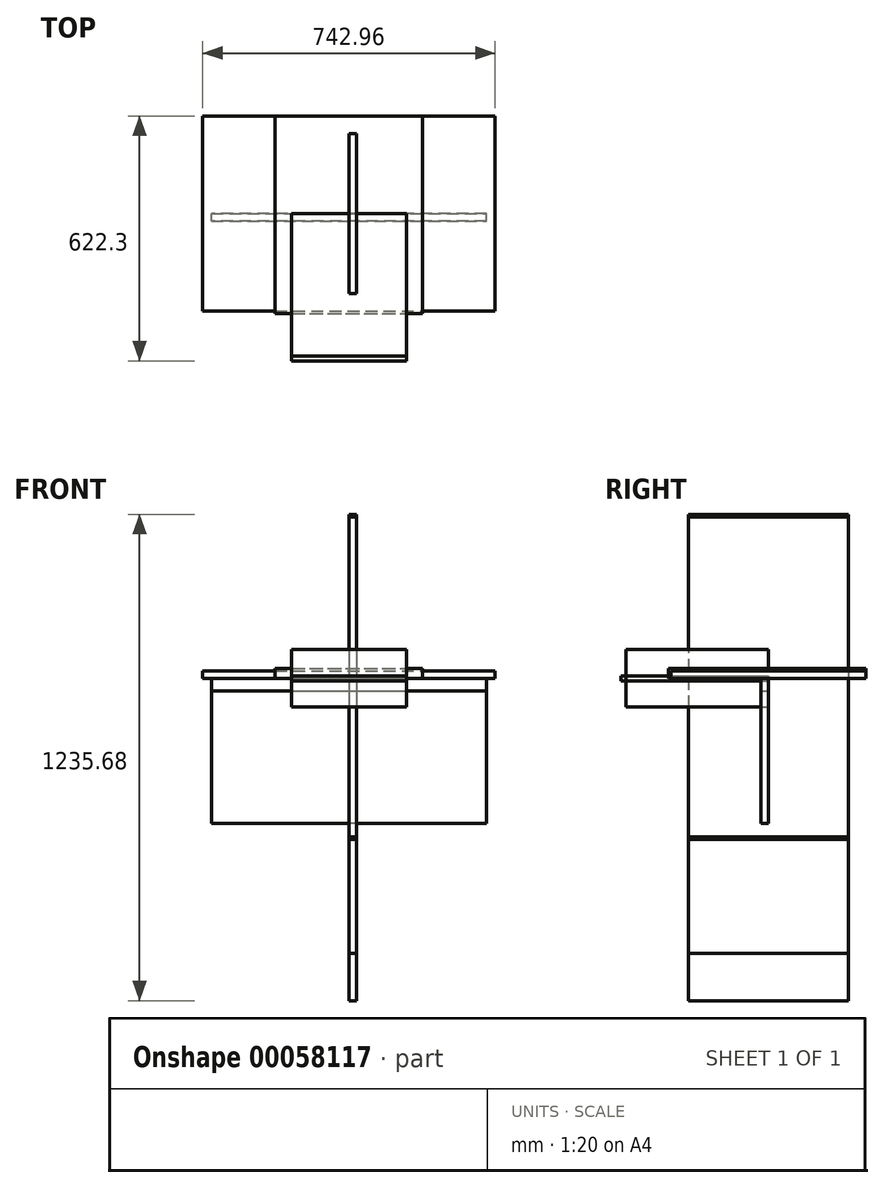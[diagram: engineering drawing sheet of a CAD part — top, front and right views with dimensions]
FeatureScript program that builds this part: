
annotation { "Feature Type Name" : "Feature", "Feature Type Description" : "" }
export const myFeature = defineFeature(function(context is Context, id is Id, definition is map)
    precondition{}
    {
        {
            var Q0;
            Q0=qCreatedBy(makeId("Top.planeOp"),FACE);
            var sketch = newSketch(context, id + "F0", { "sketchPlane" : qUnion([Q0])});
            skLineSegment(sketch, "E0.bottom", {"start": v(-371.48, 247.65) * mm, "end": v(371.48, 247.65) * mm});
            skLineSegment(sketch, "E0.top", {"start": v(-371.48, -247.65) * mm, "end": v(371.48, -247.65) * mm});
            skLineSegment(sketch, "E0.left", {"start": v(-371.48, 247.65) * mm, "end": v(-371.48, -247.65) * mm});
            skLineSegment(sketch, "E0.right", {"start": v(371.48, 247.65) * mm, "end": v(371.48, -247.65) * mm});
            skSolve(sketch);
        }
        {
            var Q0;
            Q0=makeQuery(id+"F0.imprint","IMPRINT",FACE,{"disambiguationData":[TD([[makeQuery(id+"F0.imprint","IMPRINT",EDGE,{"derivedFrom":sQuery(id+"F0.wireOp",EDGE,"E0.bottom")}),-1.0]])]});
            extrude(context, id + "F1", {"entities" : qUnion([Q0]), "depth" : 19.05 * mm});
        }
        {
            var Q0;
            Q0=qCreatedBy(makeId("Front.planeOp"),FACE);
            var sketch = newSketch(context, id + "F2", { "sketchPlane" : qUnion([Q0])});
            skLineSegment(sketch, "E1.bottom", {"start": v(-349.25, 0) * mm, "end": v(349.25, 0) * mm});
            skLineSegment(sketch, "E1.top", {"start": v(-349.25, -31.75) * mm, "end": v(349.25, -31.75) * mm});
            skLineSegment(sketch, "E1.left", {"start": v(-349.25, 0) * mm, "end": v(-349.25, -31.75) * mm});
            skLineSegment(sketch, "E1.right", {"start": v(349.25, 0) * mm, "end": v(349.25, -31.75) * mm});
            skSolve(sketch);
        }
        {
            var Q0;
            Q0=makeQuery(id+"F2.imprint","IMPRINT",FACE,{"disambiguationData":[TD([[makeQuery(id+"F2.imprint","IMPRINT",EDGE,{"derivedFrom":sQuery(id+"F2.wireOp",EDGE,"E1.bottom")}),-1.0]])]});
            extrude(context, id + "F3", {"entities" : qUnion([Q0]), "depth" : 19.05 * mm});
        }
        {
            var Q0;
            Q0=qCreatedBy(makeId("Right.planeOp"),FACE);
            var sketch = newSketch(context, id + "F4", { "sketchPlane" : qUnion([Q0])});
            skLineSegment(sketch, "E2.bottom", {"start": v(203.2, 0) * mm, "end": v(-203.2, 0) * mm});
            skLineSegment(sketch, "E2.top", {"start": v(203.2, -819.15) * mm, "end": v(-203.2, -819.15) * mm});
            skLineSegment(sketch, "E2.left", {"start": v(203.2, 0) * mm, "end": v(203.2, -819.15) * mm});
            skLineSegment(sketch, "E2.right", {"start": v(-203.2, 0) * mm, "end": v(-203.2, -819.15) * mm});
            skSolve(sketch);
        }
        {
            var Q0;
            Q0=makeQuery(id+"F4.imprint","IMPRINT",FACE,{"disambiguationData":[TD([[makeQuery(id+"F4.imprint","IMPRINT",EDGE,{"derivedFrom":sQuery(id+"F4.wireOp",EDGE,"E2.bottom")}),1.0]])]});
            extrude(context, id + "F5", {"entities" : qUnion([Q0]), "depth" : 19.05 * mm});
        }
        {
            var Q0;
            Q0=qCreatedBy(makeId("Right.planeOp"),FACE);
            var sketch = newSketch(context, id + "F6", { "sketchPlane" : qUnion([Q0])});
            skLineSegment(sketch, "E3.bottom", {"start": v(203.2, 0) * mm, "end": v(-203.2, 0) * mm});
            skLineSegment(sketch, "E3.top", {"start": v(203.2, -698.5) * mm, "end": v(-203.2, -698.5) * mm});
            skLineSegment(sketch, "E3.left", {"start": v(203.2, 0) * mm, "end": v(203.2, -698.5) * mm});
            skLineSegment(sketch, "E3.right", {"start": v(-203.2, 0) * mm, "end": v(-203.2, -698.5) * mm});
            skSolve(sketch);
        }
        {
            var Q0;
            Q0=makeQuery(id+"F6.imprint","IMPRINT",FACE,{"disambiguationData":[TD([[makeQuery(id+"F6.imprint","IMPRINT",EDGE,{"derivedFrom":sQuery(id+"F6.wireOp",EDGE,"E3.bottom")}),1.0]])]});
            extrude(context, id + "F7", {"entities" : qUnion([Q0]), "depth" : 19.05 * mm});
        }
        {
            var Q0;
            Q0=qCreatedBy(makeId("Front.planeOp"),FACE);
            var sketch = newSketch(context, id + "F8", { "sketchPlane" : qUnion([Q0])});
            skLineSegment(sketch, "E4.bottom", {"start": v(349.69, 0) * mm, "end": v(-348.81, 0) * mm});
            skLineSegment(sketch, "E4.top", {"start": v(349.69, -368.3) * mm, "end": v(-348.81, -368.3) * mm});
            skLineSegment(sketch, "E4.left", {"start": v(349.69, 0) * mm, "end": v(349.69, -368.3) * mm});
            skLineSegment(sketch, "E4.right", {"start": v(-348.81, 0) * mm, "end": v(-348.81, -368.3) * mm});
            skSolve(sketch);
        }
        {
            var Q0;
            Q0=makeQuery(id+"F8.imprint","IMPRINT",FACE,{"disambiguationData":[TD([[makeQuery(id+"F8.imprint","IMPRINT",EDGE,{"derivedFrom":sQuery(id+"F8.wireOp",EDGE,"E4.bottom")}),1.0]])]});
            extrude(context, id + "F9", {"entities" : qUnion([Q0]), "depth" : 19.05 * mm});
        }
        {
            var Q0;
            Q0=qCreatedBy(makeId("Top.planeOp"),FACE);
            var sketch = newSketch(context, id + "F10", { "sketchPlane" : qUnion([Q0])});
            skLineSegment(sketch, "E5.bottom", {"start": v(-187.33, 247.65) * mm, "end": v(187.33, 247.65) * mm});
            skLineSegment(sketch, "E5.top", {"start": v(-187.33, -254) * mm, "end": v(187.33, -254) * mm});
            skLineSegment(sketch, "E5.left", {"start": v(-187.33, 247.65) * mm, "end": v(-187.33, -254) * mm});
            skLineSegment(sketch, "E5.right", {"start": v(187.33, 247.65) * mm, "end": v(187.33, -254) * mm});
            skSolve(sketch);
        }
        {
            var Q0;
            Q0=makeQuery(id+"F10.imprint","IMPRINT",FACE,{"disambiguationData":[TD([[makeQuery(id+"F10.imprint","IMPRINT",EDGE,{"derivedFrom":sQuery(id+"F10.wireOp",EDGE,"E5.bottom")}),-1.0]])]});
            extrude(context, id + "F11", {"entities" : qUnion([Q0]), "depth" : 25.4 * mm});
        }
        {
            var Q0;
            Q0=qCreatedBy(makeId("Right.planeOp"),FACE);
            var sketch = newSketch(context, id + "F12", { "sketchPlane" : qUnion([Q0])});
            skLineSegment(sketch, "E6.bottom", {"start": v(-203.2, 416.53) * mm, "end": v(203.2, 416.53) * mm});
            skLineSegment(sketch, "E6.top", {"start": v(-203.2, -402.62) * mm, "end": v(203.2, -402.62) * mm});
            skLineSegment(sketch, "E6.left", {"start": v(-203.2, 416.53) * mm, "end": v(-203.2, -402.62) * mm});
            skLineSegment(sketch, "E6.right", {"start": v(203.2, 416.53) * mm, "end": v(203.2, -402.62) * mm});
            skSolve(sketch);
        }
        {
            var Q0;
            Q0=makeQuery(id+"F12.imprint","IMPRINT",FACE,{"disambiguationData":[TD([[makeQuery(id+"F12.imprint","IMPRINT",EDGE,{"derivedFrom":sQuery(id+"F12.wireOp",EDGE,"E6.bottom")}),-1.0]])]});
            extrude(context, id + "F13", {"entities" : qUnion([Q0]), "depth" : 19.05 * mm});
        }
        {
            var Q0;
            Q0=qCreatedBy(makeId("Right.planeOp"),FACE);
            var sketch = newSketch(context, id + "F14", { "sketchPlane" : qUnion([Q0])});
            skLineSegment(sketch, "E7.bottom", {"start": v(203.2, 409.57) * mm, "end": v(-203.2, 409.57) * mm});
            skLineSegment(sketch, "E7.top", {"start": v(203.2, -409.58) * mm, "end": v(-203.2, -409.58) * mm});
            skLineSegment(sketch, "E7.left", {"start": v(203.2, 409.57) * mm, "end": v(203.2, -409.58) * mm});
            skLineSegment(sketch, "E7.right", {"start": v(-203.2, 409.57) * mm, "end": v(-203.2, -409.58) * mm});
            skSolve(sketch);
        }
        {
            var Q0;
            Q0 = qSketchRegion(id + "F14", true);
            extrude(context, id + "F15", {"entities" : qUnion([Q0]), "depth" : 19.05 * mm});
        }
        {
            var Q0;
            Q0=qCreatedBy(makeId("Front.planeOp"),FACE);
            var sketch = newSketch(context, id + "F16", { "sketchPlane" : qUnion([Q0])});
            skLineSegment(sketch, "E8.bottom", {"start": v(-146.05, 73.02) * mm, "end": v(146.05, 73.03) * mm});
            skLineSegment(sketch, "E8.top", {"start": v(-146.05, -73.03) * mm, "end": v(146.05, -73.02) * mm});
            skLineSegment(sketch, "E8.left", {"start": v(-146.05, 73.02) * mm, "end": v(-146.05, -73.03) * mm});
            skLineSegment(sketch, "E8.right", {"start": v(146.05, 73.03) * mm, "end": v(146.05, -73.02) * mm});
            skSolve(sketch);
        }
        {
            var Q0;
            Q0=makeQuery(id+"F16.imprint","IMPRINT",FACE,{"disambiguationData":[TD([[makeQuery(id+"F16.imprint","IMPRINT",EDGE,{"derivedFrom":sQuery(id+"F16.wireOp",EDGE,"E8.bottom")}),-1.0]])]});
            extrude(context, id + "F17", {"entities" : qUnion([Q0]), "depth" : 361.95 * mm});
        }
        {
            var Q0;
            Q0=qCreatedBy(makeId("Front.planeOp"),FACE);
            var sketch = newSketch(context, id + "F18", { "sketchPlane" : qUnion([Q0])});
            skLineSegment(sketch, "E9.bottom", {"start": v(-146.05, 6.35) * mm, "end": v(146.05, 6.35) * mm});
            skLineSegment(sketch, "E9.top", {"start": v(-146.05, -6.35) * mm, "end": v(146.05, -6.35) * mm});
            skLineSegment(sketch, "E9.left", {"start": v(-146.05, 6.35) * mm, "end": v(-146.05, -6.35) * mm});
            skLineSegment(sketch, "E9.right", {"start": v(146.05, 6.35) * mm, "end": v(146.05, -6.35) * mm});
            skSolve(sketch);
        }
        {
            var Q0;
            Q0=makeQuery(id+"F18.imprint","IMPRINT",FACE,{"disambiguationData":[TD([[makeQuery(id+"F18.imprint","IMPRINT",EDGE,{"derivedFrom":sQuery(id+"F18.wireOp",EDGE,"E9.bottom")}),-1.0]])]});
            extrude(context, id + "F19", {"entities" : qUnion([Q0]), "depth" : 374.65 * mm});
        }
    });
